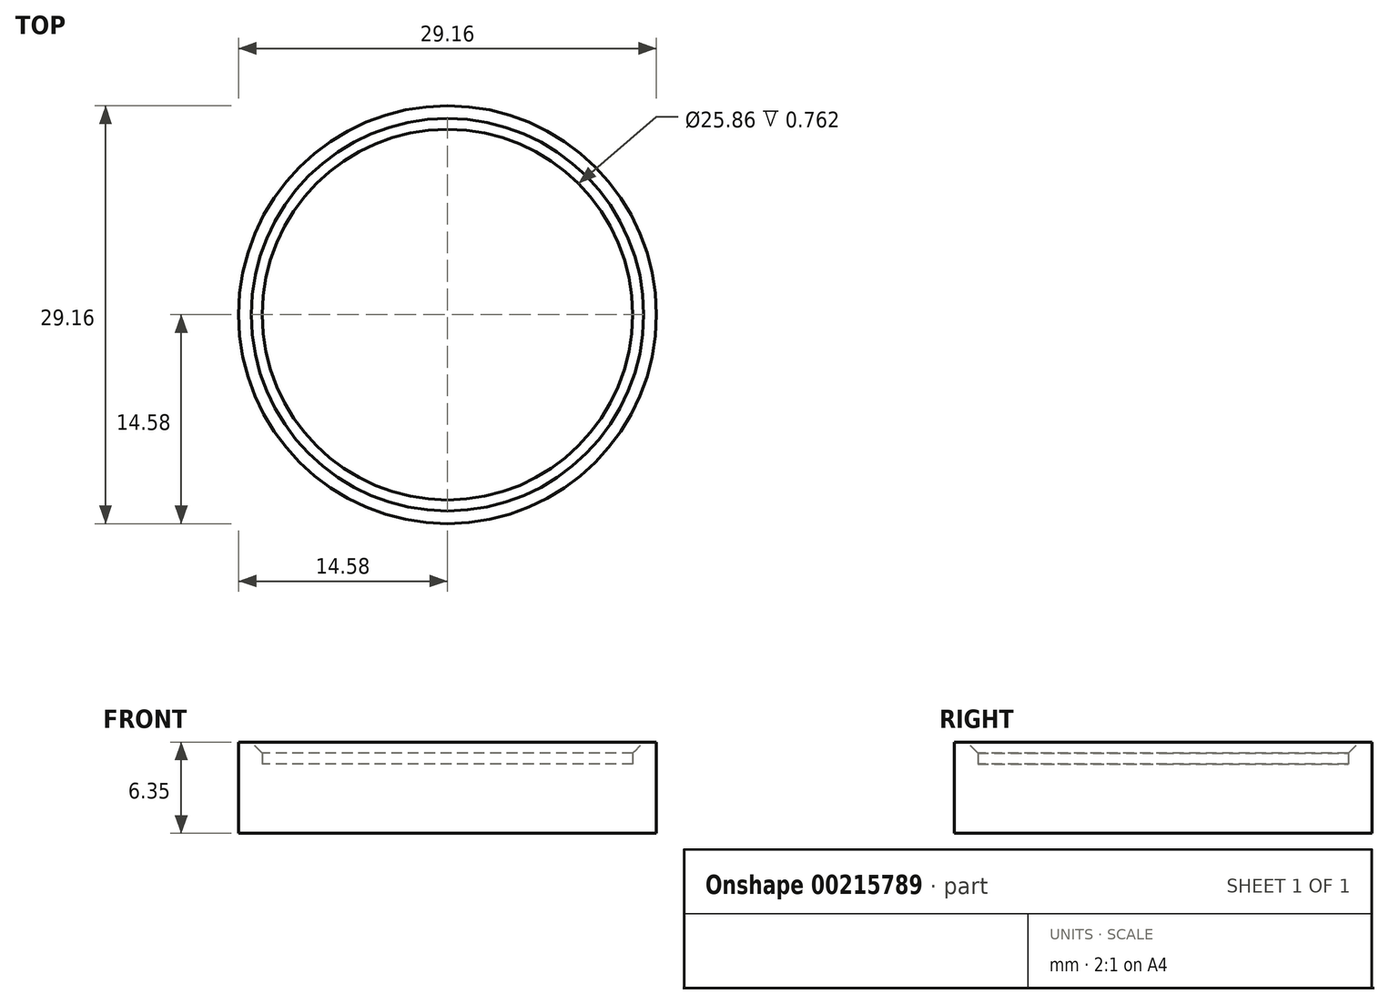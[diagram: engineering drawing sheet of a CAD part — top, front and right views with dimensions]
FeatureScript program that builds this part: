
annotation { "Feature Type Name" : "Feature", "Feature Type Description" : "" }
export const myFeature = defineFeature(function(context is Context, id is Id, definition is map)
    precondition{}
    {
        {
            var Q0;
            Q0=qCreatedBy(makeId("Top.planeOp"),FACE);
            var sketch = newSketch(context, id + "F0", { "sketchPlane" : qUnion([Q0])});
            skCircle(sketch, "E0", {"center": v(0, 0) * mm, "radius": 14.58 * mm});
            skSolve(sketch);
        }
        {
            var Q0;
            Q0=makeQuery(id+"F0.imprint","IMPRINT",FACE,{"disambiguationData":[TD([[makeQuery(id+"F0.imprint","IMPRINT",EDGE,{"derivedFrom":sQuery(id+"F0.wireOp",EDGE,"E0")}),1.0]])]});
            extrude(context, id + "F1", {"entities" : qUnion([Q0]), "depth" : 4.83 * mm});
        }
        {
            var Q0;
            Q0=makeQuery(id+"F1.opExtrude","CAP_FACE",FACE,{"disambiguationData":[OSD([sQuery(id+"F0.wireOp",EDGE,"E0")])],"isStart":false});
            var sketch = newSketch(context, id + "F2", { "sketchPlane" : qUnion([Q0])});
            skCircle(sketch, "E1", {"center": v(0, 0) * mm, "radius": 14.58 * mm});
            skCircle(sketch, "E2", {"center": v(0, 0) * mm, "radius": 12.93 * mm});
            skSolve(sketch);
        }
        {
            var Q0;
            Q0=qSketchRegion(id+"F2",true);
            extrude(context, id + "F3", {"entities" : qUnion([Q0]), "operationType" : NewBodyOperationType.ADD, "depth" : 1.52 * mm});
        }
        {
            var Q0;
            Q0=makeQuery(id+"F3.opExtrude","CAP_EDGE",EDGE,{"disambiguationData":[OSD([sQuery(id+"F2.wireOp",EDGE,"E2")])],"isStart":false});
            chamfer(context, id + "F4", {"entities" : qUnion([Q0]), "width" : 0.76 * mm, "tangentPropagation" : true});
        }
    });
